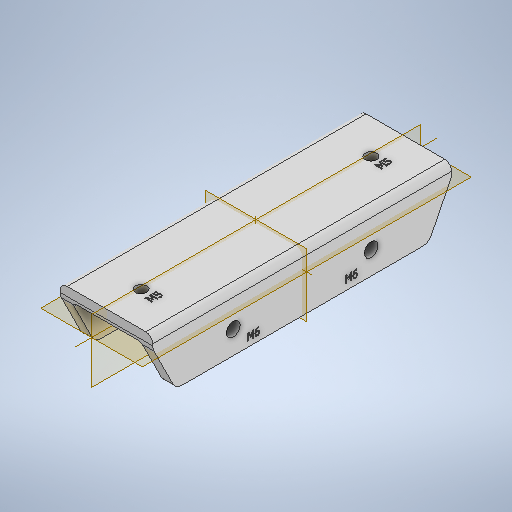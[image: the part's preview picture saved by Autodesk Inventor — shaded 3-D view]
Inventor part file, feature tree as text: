
AUTODESK INVENTOR PART (.ipt)
format: ipt  version: 2025 (Build 290162000, 162)  size: 530,944 bytes
history: native  units: mm
features: sketch x5, chamfer x2, fillet x2, hole x2, emboss x2, extrude x1, mirror x1
ambient origin geometry x8: Origin, YZ Plane, XZ Plane, XY Plane, X Axis, Y Axis, Z Axis, Center Point
bodies: Solid1 (feature_tree)
feature tree (15):
  extrude  "Extrusion1"  Depth=30.2mm
  chamfer  "Chamfer1"  Distance=130.0mm
  chamfer  "Chamfer2"  Distance=10.0mm Angle=60.0deg
  fillet  "Fillet1"  Radius=5.0mm
  hole  "Hole1"  [1 undecoded]
  hole  "Hole2"  [1 undecoded]
  mirror  "Mirror3"
  emboss  "Emboss1"
  emboss  "Emboss2"
  fillet  "Fillet4"  Radius=50.0mm
  sketch  "Sketch1"  dims[d0=20.0mm d1=30.2mm]
  sketch  "Sketch2"  dims[d2=5.0mm]
  sketch  "Sketch3"  dims[d3=2.0mm]
  sketch  "Sketch4"  dims[d4=3.0mm d5=130.0mm d6=0.0mm d7=20.0mm d8=10.0mm d9=60.0deg]
  sketch  "Sketch5"  dims[d10=20.0mm d11=10.0mm d12=60.0deg d13=5.0mm d14=6.0mm d15=6.0mm d16=4.0mm d17=2.0mm d18=90.0deg d19=8.0mm d20=20.594885mm d21=10.0mm d22=30.0mm d23=5.0mm d24=6.0mm d25=4.0mm d26=2.0mm d27=90.0deg d28=8.0mm d29=20.594885mm d30=50.0mm d31=1.5mm d32=0.0mm d33=1.5mm d34=0.0mm d42=4.0mm d41=0.0mm d43=0.0mm d44=0.0mm]
note: 2 required parameter values undecoded (feature->parameter linkage not recoverable at this tier; creation-order binding heuristic only, values carry confidence <= 0.55)
